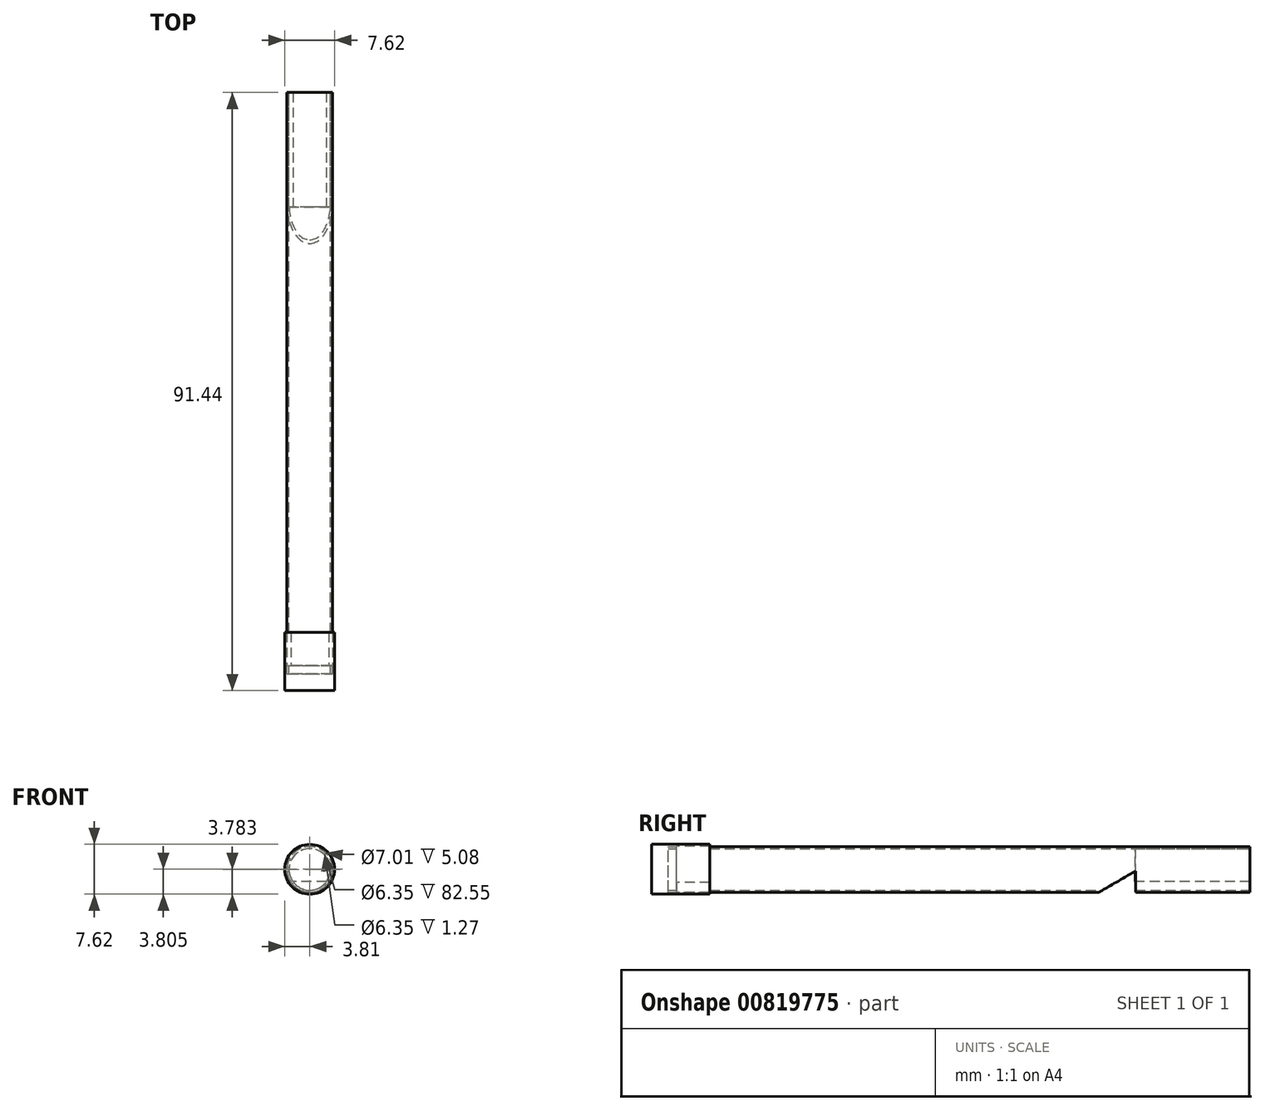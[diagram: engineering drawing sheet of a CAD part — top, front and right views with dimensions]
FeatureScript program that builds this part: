
annotation { "Feature Type Name" : "Feature", "Feature Type Description" : "" }
export const myFeature = defineFeature(function(context is Context, id is Id, definition is map)
    precondition{}
    {
        {
            var Q0;
            Q0=qCreatedBy(makeId("Front.planeOp"),FACE);
            var sketch = newSketch(context, id + "F0", { "sketchPlane" : qUnion([Q0])});
            skCircle(sketch, "E0", {"center": v(0, 3.5) * mm, "radius": 3.5 * mm});
            skCircle(sketch, "E1", {"center": v(0, 3.5) * mm, "radius": 3.18 * mm});
            skSolve(sketch);
        }
        {
            var Q0;
            Q0=qCreatedBy(makeId("Right.planeOp"),FACE);
            var sketch = newSketch(context, id + "F1", { "sketchPlane" : qUnion([Q0])});
            skLineSegment(sketch, "E2", {"start": v(-17.48, 0) * mm, "end": v(-17.48, -3.24) * mm});
            skLineSegment(sketch, "E3", {"start": v(-17.48, -3.24) * mm, "end": v(-23.08, 0) * mm});
            skLineSegment(sketch, "E4", {"start": v(-23.08, 0) * mm, "end": v(-17.48, 0) * mm});
            skLineSegment(sketch, "E5.MirrorCS", {"start": v(-17.48, 3.24) * mm, "end": v(-23.08, 0) * mm});
            skLineSegment(sketch, "E6.MirrorCS", {"start": v(-17.48, 0) * mm, "end": v(-17.48, 3.24) * mm});
            skSolve(sketch);
        }
        {
            var Q0;
            Q0=qSketchRegion(id+"F0",true);
            extrude(context, id + "F2", {"entities" : qUnion([Q0]), "depth" : 88.9 * mm, "offsetDistance" : 25.4 * mm});
        }
        {
            var Q0;
            Q0=qSketchRegion(id+"F0",true);
            extrude(context, id + "F3", {"entities" : qUnion([Q0]), "operationType" : NewBodyOperationType.ADD, "depth" : 25.4 * mm, "offsetDistance" : 25.4 * mm});
        }
        {
            var Q0;
            Q0=qSketchRegion(id+"F1",true);
            extrude(context, id + "F4", {"entities" : qUnion([Q0]), "operationType" : NewBodyOperationType.REMOVE, "oppositeDirection" : true, "depth" : 25.4 * mm, "offsetDistance" : 25.4 * mm, "hasSecondDirection" : true, "secondDirectionOppositeDirection" : true, "secondDirectionDepth" : -25.4 * mm});
        }
        {
            var Q0;
            Q0=qCreatedBy(makeId("Front.planeOp"),FACE);
            var sketch = newSketch(context, id + "F5", { "sketchPlane" : qUnion([Q0])});
            skCircle(sketch, "E7", {"center": v(0, 3.5) * mm, "radius": 3.17 * mm});
            skSolve(sketch);
        }
        {
            var Q0;
            Q0=qSketchRegion(id+"F5",true);
            extrude(context, id + "F6", {"entities" : qUnion([Q0]), "depth" : 17.53 * mm, "offsetDistance" : 25.4 * mm});
        }
        {
            var Q0;
            Q0=makeQuery(id+"F6.opExtrude","CAP_FACE",FACE,{"disambiguationData":[OSD([sQuery(id+"F5.wireOp",EDGE,"E7")])],"isStart":false});
            var sketch = newSketch(context, id + "F7", { "sketchPlane" : qUnion([Q0])});
            skLineSegment(sketch, "E8", {"start": v(2.54, 1.62) * mm, "end": v(-2.54, 1.62) * mm});
            skArc(sketch, "E9", {"start": v(-2.54, 1.62) * mm, "mid": v(0, 0.34) * mm, "end": v(2.54, 1.62) * mm});
            skSolve(sketch);
        }
        {
            var Q0;
            Q0=qSketchRegion(id+"F7",true);
            extrude(context, id + "F8", {"entities" : qUnion([Q0]), "operationType" : NewBodyOperationType.REMOVE, "oppositeDirection" : true, "depth" : 17.78 * mm, "offsetDistance" : 25.4 * mm});
        }
        {
            var Q0;
            Q0=qCreatedBy(makeId("Front.planeOp"),FACE);
            cPlane(context, id + "F9", {"entities" : qUnion([Q0]), "cplaneType" : CPlaneType.OFFSET, "offset" : 88.9 * mm, "width" : 152.4 * mm, "height" : 152.4 * mm});
        }
        {
            var Q0;
            Q0=qCreatedBy(id+"F9.planeOp",FACE);
            var sketch = newSketch(context, id + "F10", { "sketchPlane" : qUnion([Q0])});
            skCircle(sketch, "E10", {"center": v(0, 3.52) * mm, "radius": 3.8 * mm});
            skSolve(sketch);
        }
        {
            var Q0;
            Q0=qSketchRegion(id+"F10",true);
            extrude(context, id + "F11", {"entities" : qUnion([Q0]), "depth" : 2.54 * mm, "offsetDistance" : 25.4 * mm, "hasSecondDirection" : true, "secondDirectionOppositeDirection" : true, "secondDirectionDepth" : 6.35 * mm});
        }
        {
            var Q0;
            Q0=qCreatedBy(id+"F9.planeOp",FACE);
            var sketch = newSketch(context, id + "F12", { "sketchPlane" : qUnion([Q0])});
            skCircle(sketch, "E11", {"center": v(0, 3.52) * mm, "radius": 3.5 * mm});
            skSolve(sketch);
        }
        {
            var Q0;
            Q0=qSketchRegion(id+"F12",true);
            extrude(context, id + "F13", {"entities" : qUnion([Q0]), "operationType" : NewBodyOperationType.REMOVE, "oppositeDirection" : true, "depth" : 6.35 * mm, "offsetDistance" : 25.4 * mm, "hasSecondDirection" : true, "secondDirectionOppositeDirection" : true, "secondDirectionDepth" : 1.27 * mm});
        }
    });
